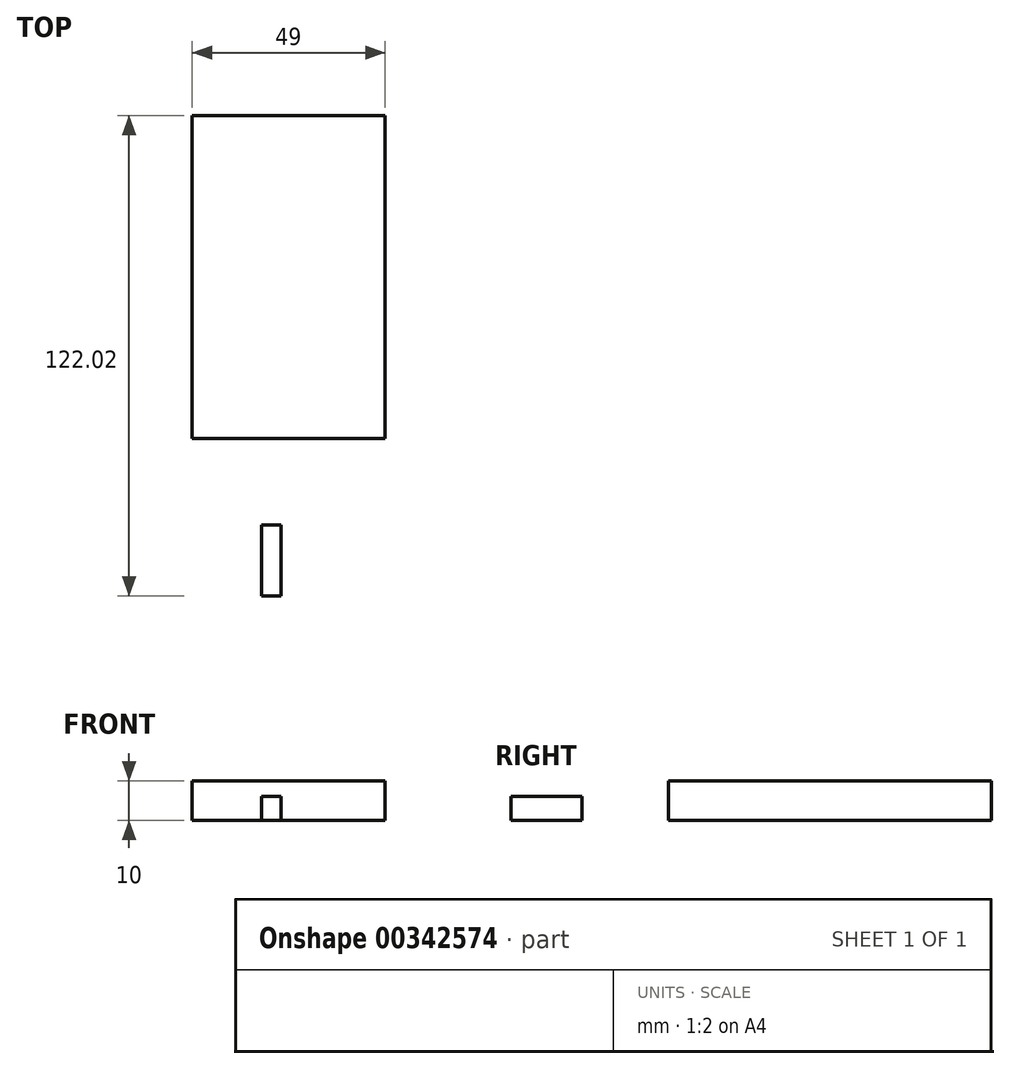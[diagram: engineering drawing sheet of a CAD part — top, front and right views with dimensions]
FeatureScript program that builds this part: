
annotation { "Feature Type Name" : "Feature", "Feature Type Description" : "" }
export const myFeature = defineFeature(function(context is Context, id is Id, definition is map)
    precondition{}
    {
        {
            var Q0;
            Q0=qCreatedBy(makeId("Top.planeOp"),FACE);
            var sketch = newSketch(context, id + "F0", { "sketchPlane" : qUnion([Q0])});
            skLineSegment(sketch, "E0.bottom", {"start": v(-198.61, -139.13) * mm, "end": v(-149.61, -139.13) * mm});
            skLineSegment(sketch, "E0.top", {"start": v(-198.61, -57.13) * mm, "end": v(-149.61, -57.13) * mm});
            skLineSegment(sketch, "E0.left", {"start": v(-198.61, -139.13) * mm, "end": v(-198.61, -57.13) * mm});
            skLineSegment(sketch, "E0.right", {"start": v(-149.61, -139.13) * mm, "end": v(-149.61, -57.13) * mm});
            skSolve(sketch);
        }
        {
            var Q0;
            Q0 = qSketchRegion(id + "F0", true);
            extrude(context, id + "F1", {"entities" : qUnion([Q0]), "depth" : 10 * mm});
        }
        {
            var Q0;
            Q0=qCreatedBy(makeId("Top.planeOp"),FACE);
            var sketch = newSketch(context, id + "F2", { "sketchPlane" : qUnion([Q0])});
            skLineSegment(sketch, "E1", {"start": v(-181.04, -161.15) * mm, "end": v(-176.04, -161.15) * mm});
            skLineSegment(sketch, "E2", {"start": v(-181.04, -161.15) * mm, "end": v(-181.04, -179.15) * mm});
            skLineSegment(sketch, "E3", {"start": v(-176.04, -161.15) * mm, "end": v(-176.04, -179.15) * mm});
            skLineSegment(sketch, "E4", {"start": v(-176.04, -179.15) * mm, "end": v(-181.04, -179.15) * mm});
            skSolve(sketch);
        }
        {
            var Q0;
            Q0 = qSketchRegion(id + "F2", true);
            extrude(context, id + "F3", {"entities" : qUnion([Q0]), "depth" : 6 * mm});
        }
    });
